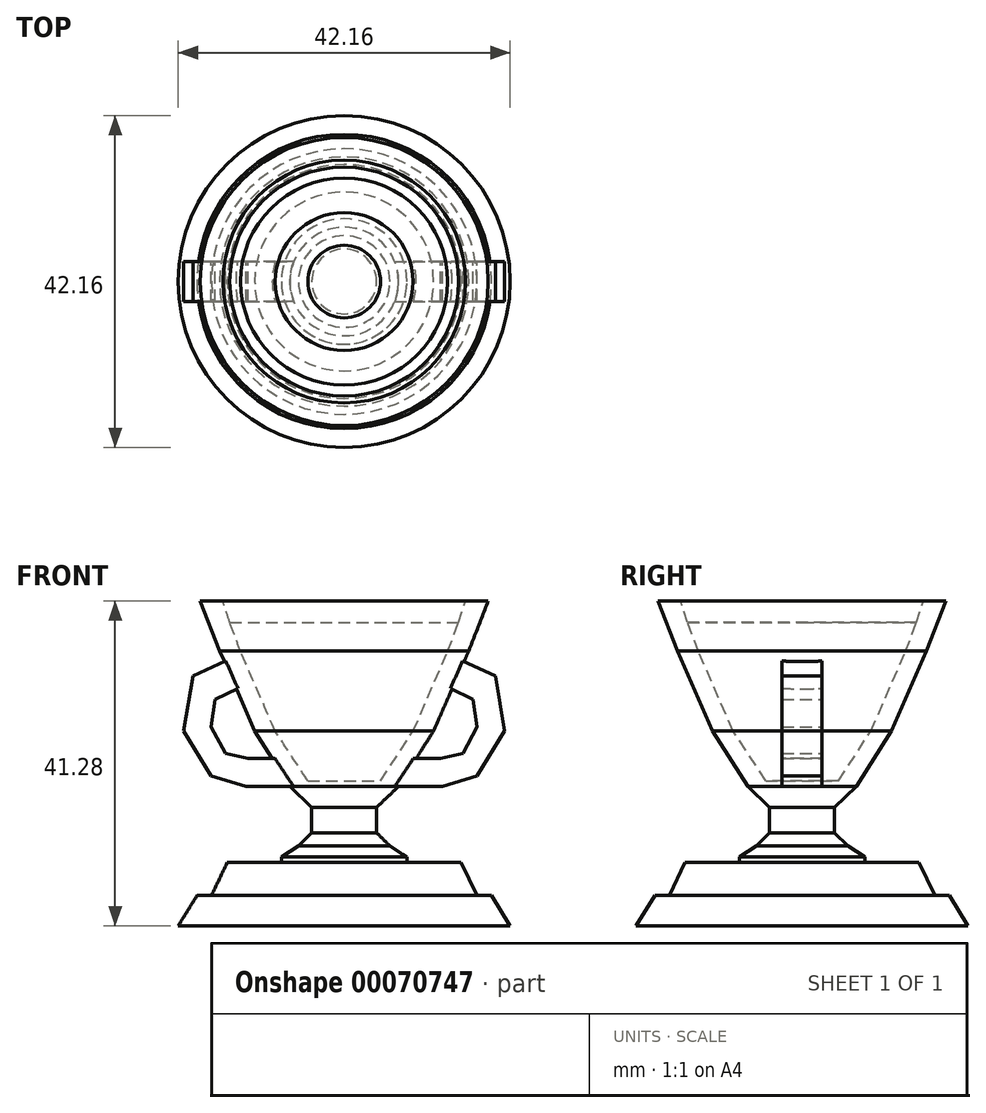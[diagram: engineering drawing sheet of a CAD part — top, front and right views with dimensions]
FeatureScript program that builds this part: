
annotation { "Feature Type Name" : "Feature", "Feature Type Description" : "" }
export const myFeature = defineFeature(function(context is Context, id is Id, definition is map)
    precondition{}
    {
        {
            var Q0;
            Q0=qCreatedBy(makeId("Front.planeOp"),FACE);
            var sketch = newSketch(context, id + "F0", { "sketchPlane" : qUnion([Q0])});
            skLineSegment(sketch, "E0", {"start": v(0, -7.24) * mm, "end": v(-14.85, -7.24) * mm});
            skLineSegment(sketch, "E1", {"start": v(-14.85, -7.24) * mm, "end": v(-16.86, -11.46) * mm});
            skLineSegment(sketch, "E2", {"start": v(-16.86, -11.46) * mm, "end": v(-18.7, -11.46) * mm});
            skLineSegment(sketch, "E3", {"start": v(-18.7, -11.46) * mm, "end": v(-21.08, -15.3) * mm});
            skLineSegment(sketch, "E4", {"start": v(-21.08, -15.3) * mm, "end": v(0, -15.3) * mm});
            skLineSegment(sketch, "E5", {"start": v(0, -15.3) * mm, "end": v(0, -7.24) * mm});
            skSolve(sketch);
        }
        {
            var Q0;
            Q0 = qSketchRegion(id + "F0", true);
            var Q1;
            Q1=sQuery(id+"F0.wireOp",EDGE,"E5");
            revolve(context, id + "F1", {"entities" : qUnion([Q0]), "axis" : qUnion([Q1]), "revolveType" : RevolveType.FULL});
        }
        {
            var Q0;
            Q0=qCreatedBy(makeId("Front.planeOp"),FACE);
            var sketch = newSketch(context, id + "F2", { "sketchPlane" : qUnion([Q0])});
            skLineSegment(sketch, "E6", {"start": v(0, -7.94) * mm, "end": v(-4.27, -7.94) * mm});
            skLineSegment(sketch, "E7", {"start": v(-4.27, -7.94) * mm, "end": v(-7.97, -7.94) * mm});
            skLineSegment(sketch, "E8", {"start": v(-7.97, -7.94) * mm, "end": v(-7.97, -6.56) * mm});
            skLineSegment(sketch, "E9", {"start": v(-7.97, -6.56) * mm, "end": v(-5.81, -5.17) * mm});
            skLineSegment(sketch, "E10", {"start": v(-5.81, -5.17) * mm, "end": v(-4.12, -3.47) * mm});
            skLineSegment(sketch, "E11", {"start": v(-4.12, -3.47) * mm, "end": v(-4.12, -0.24) * mm});
            skLineSegment(sketch, "E12", {"start": v(-4.12, -0.24) * mm, "end": v(-6.9, 2.38) * mm});
            skLineSegment(sketch, "E13", {"start": v(-6.9, 2.38) * mm, "end": v(-11.36, 9.47) * mm});
            skLineSegment(sketch, "E14", {"start": v(-11.36, 9.47) * mm, "end": v(-15.83, 19.65) * mm});
            skLineSegment(sketch, "E15", {"start": v(-15.83, 19.65) * mm, "end": v(-18.3, 25.97) * mm});
            skLineSegment(sketch, "E16", {"start": v(-18.3, 25.97) * mm, "end": v(0, 25.97) * mm});
            skLineSegment(sketch, "E17", {"start": v(0, 25.97) * mm, "end": v(0, -7.94) * mm});
            skSolve(sketch);
        }
        {
            var Q0;
            Q0 = qSketchRegion(id + "F2", true);
            var Q1;
            Q1=sQuery(id+"F2.wireOp",EDGE,"E17");
            revolve(context, id + "F3", {"operationType" : NewBodyOperationType.ADD, "entities" : qUnion([Q0]), "axis" : qUnion([Q1]), "revolveType" : RevolveType.FULL});
        }
        {
            var Q0;
            Q0=qCreatedBy(makeId("Front.planeOp"),FACE);
            var sketch = newSketch(context, id + "F4", { "sketchPlane" : qUnion([Q0])});
            skLineSegment(sketch, "E18", {"start": v(-11.96, 15.66) * mm, "end": v(-16.37, 13.46) * mm});
            skLineSegment(sketch, "E19", {"start": v(-16.37, 13.46) * mm, "end": v(-16.89, 9.96) * mm});
            skLineSegment(sketch, "E20", {"start": v(-16.89, 9.96) * mm, "end": v(-15.07, 6.59) * mm});
            skLineSegment(sketch, "E21", {"start": v(-15.07, 6.59) * mm, "end": v(-12.22, 5.94) * mm});
            skLineSegment(sketch, "E22", {"start": v(-12.22, 5.94) * mm, "end": v(-7.17, 5.94) * mm});
            skLineSegment(sketch, "E23", {"start": v(-7.17, 5.94) * mm, "end": v(-4.58, 4) * mm});
            skLineSegment(sketch, "E24", {"start": v(-4.58, 4) * mm, "end": v(-4.58, 2.44) * mm});
            skLineSegment(sketch, "E25", {"start": v(-4.58, 2.44) * mm, "end": v(-12.48, 2.44) * mm});
            skLineSegment(sketch, "E26", {"start": v(-12.48, 2.44) * mm, "end": v(-16.89, 3.73) * mm});
            skLineSegment(sketch, "E27", {"start": v(-16.89, 3.73) * mm, "end": v(-20.39, 9.44) * mm});
            skLineSegment(sketch, "E28", {"start": v(-20.39, 9.44) * mm, "end": v(-19.22, 16.44) * mm});
            skLineSegment(sketch, "E29", {"start": v(-19.22, 16.44) * mm, "end": v(-13, 19.29) * mm});
            skLineSegment(sketch, "E30", {"start": v(-13, 19.29) * mm, "end": v(-11.96, 15.66) * mm});
            skLineSegment(sketch, "E31.MirrorCS", {"start": v(15.07, 6.59) * mm, "end": v(12.22, 5.94) * mm});
            skLineSegment(sketch, "E32.MirrorCS", {"start": v(16.89, 9.96) * mm, "end": v(15.07, 6.59) * mm});
            skLineSegment(sketch, "E33.MirrorCS", {"start": v(4.58, 2.44) * mm, "end": v(12.48, 2.44) * mm});
            skLineSegment(sketch, "E34.MirrorCS", {"start": v(12.22, 5.94) * mm, "end": v(7.17, 5.94) * mm});
            skLineSegment(sketch, "E35.MirrorCS", {"start": v(12.48, 2.44) * mm, "end": v(16.89, 3.73) * mm});
            skLineSegment(sketch, "E36.MirrorCS", {"start": v(16.89, 3.73) * mm, "end": v(20.39, 9.44) * mm});
            skLineSegment(sketch, "E37.MirrorCS", {"start": v(20.39, 9.44) * mm, "end": v(19.22, 16.44) * mm});
            skLineSegment(sketch, "E38.MirrorCS", {"start": v(19.22, 16.44) * mm, "end": v(13, 19.29) * mm});
            skLineSegment(sketch, "E39.MirrorCS", {"start": v(13, 19.29) * mm, "end": v(11.96, 15.66) * mm});
            skLineSegment(sketch, "E40.MirrorCS", {"start": v(11.96, 15.66) * mm, "end": v(16.37, 13.46) * mm});
            skLineSegment(sketch, "E41.MirrorCS", {"start": v(16.37, 13.46) * mm, "end": v(16.89, 9.96) * mm});
            skLineSegment(sketch, "E42.MirrorCS", {"start": v(7.17, 5.94) * mm, "end": v(4.58, 4) * mm});
            skLineSegment(sketch, "E43.MirrorCS", {"start": v(4.58, 4) * mm, "end": v(4.58, 2.44) * mm});
            skSolve(sketch);
        }
        {
            var Q0;
            Q0 = qSketchRegion(id + "F4", true);
            extrude(context, id + "F5", {"entities" : qUnion([Q0]), "operationType" : NewBodyOperationType.ADD, "depth" : 2.54 * mm});
        }
        {
            var Q0;
            Q0 = qSketchRegion(id + "F4", true);
            extrude(context, id + "F6", {"entities" : qUnion([Q0]), "operationType" : NewBodyOperationType.ADD, "oppositeDirection" : true, "depth" : 2.54 * mm});
        }
        {
            var Q0;
            Q0=qCreatedBy(makeId("Front.planeOp"),FACE);
            var sketch = newSketch(context, id + "F7", { "sketchPlane" : qUnion([Q0])});
            skLineSegment(sketch, "E44", {"start": v(0, 23.31) * mm, "end": v(0, 3.12) * mm});
            skLineSegment(sketch, "E45", {"start": v(0, 3.12) * mm, "end": v(-4.61, 3.12) * mm});
            skLineSegment(sketch, "E46", {"start": v(-4.61, 3.12) * mm, "end": v(-8.75, 9.44) * mm});
            skLineSegment(sketch, "E47", {"start": v(-8.75, 9.44) * mm, "end": v(-13.15, 19.54) * mm});
            skLineSegment(sketch, "E48", {"start": v(-13.15, 19.54) * mm, "end": v(-14.53, 23.24) * mm});
            skLineSegment(sketch, "E49", {"start": v(-14.53, 23.24) * mm, "end": v(-15.84, 27.32) * mm});
            skLineSegment(sketch, "E50", {"start": v(-15.84, 27.32) * mm, "end": v(0, 27.32) * mm});
            skLineSegment(sketch, "E51", {"start": v(0, 27.32) * mm, "end": v(0, 3.12) * mm});
            skSolve(sketch);
        }
        {
            var Q0;
            Q0 = qSketchRegion(id + "F7", true);
            var Q1;
            Q1=sQuery(id+"F7.wireOp",EDGE,"E51");
            revolve(context, id + "F8", {"operationType" : NewBodyOperationType.REMOVE, "entities" : qUnion([Q0]), "axis" : qUnion([Q1]), "revolveType" : RevolveType.FULL, "oppositeDirection" : true});
        }
    });
